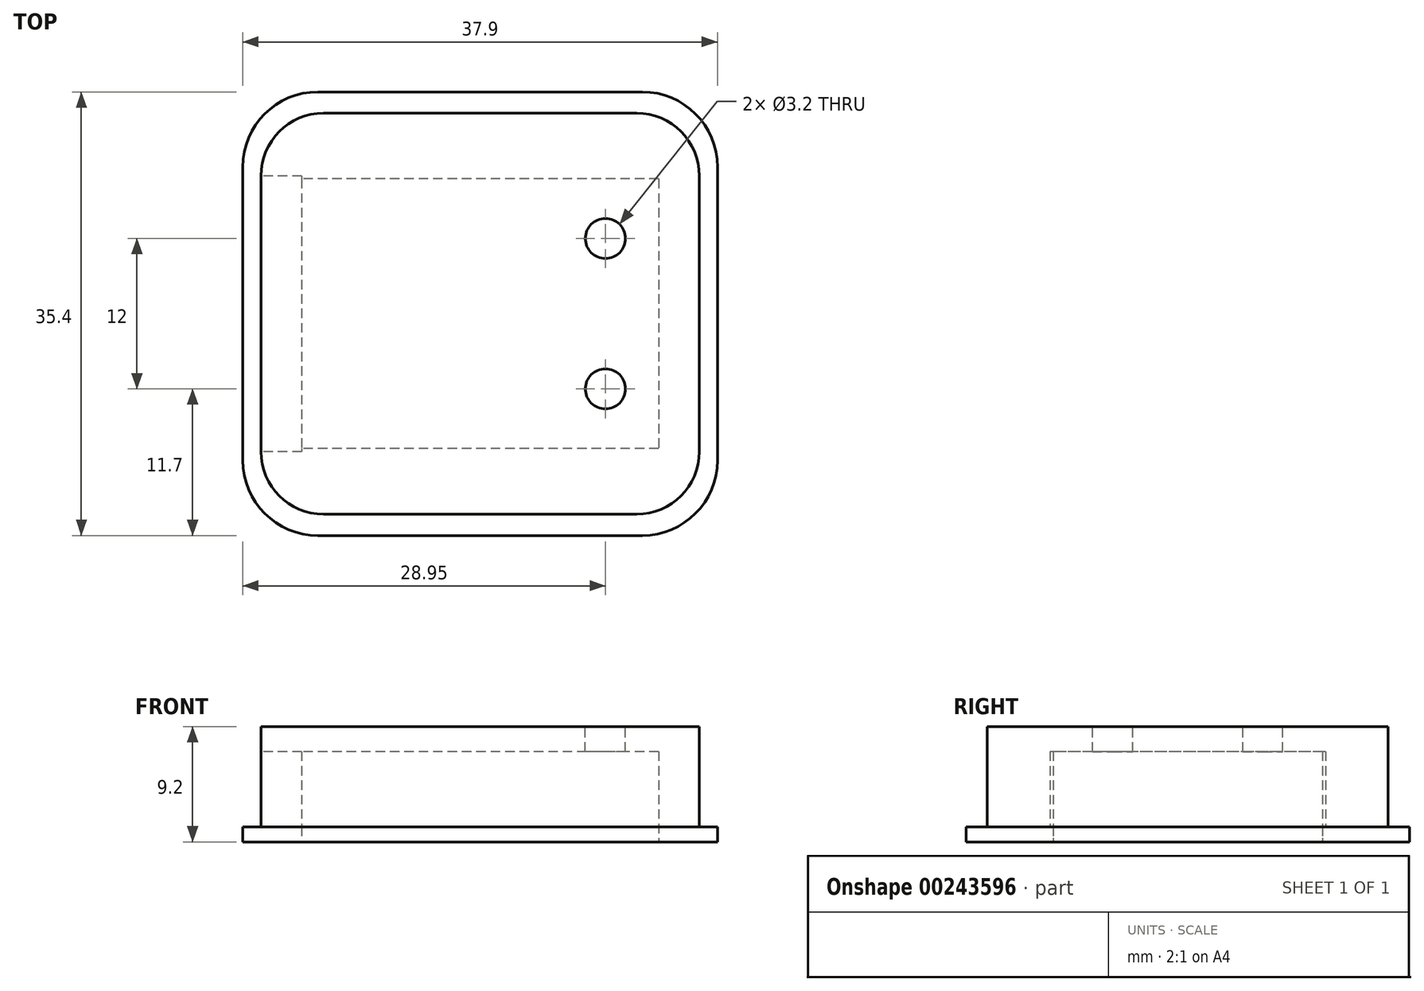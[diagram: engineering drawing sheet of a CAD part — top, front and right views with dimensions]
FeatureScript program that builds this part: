
annotation { "Feature Type Name" : "Feature", "Feature Type Description" : "" }
export const myFeature = defineFeature(function(context is Context, id is Id, definition is map)
    precondition{}
    {
        {
            var Q0;
            Q0=qCreatedBy(makeId("Top.planeOp"),FACE);
            var sketch = newSketch(context, id + "F0", { "sketchPlane" : qUnion([Q0])});
            skLineSegment(sketch, "E0.bottom", {"start": v(21.25, 20) * mm, "end": v(-21.25, 20) * mm, "construction": true});
            skLineSegment(sketch, "E0.top", {"start": v(21.25, -20) * mm, "end": v(-21.25, -20) * mm, "construction": true});
            skLineSegment(sketch, "E0.left", {"start": v(21.25, 20) * mm, "end": v(21.25, -20) * mm, "construction": true});
            skLineSegment(sketch, "E0.right", {"start": v(-21.25, 20) * mm, "end": v(-21.25, -20) * mm, "construction": true});
            skPoint(sketch, "E0.middle", {"position": v(0, 0) * mm});
            skLineSegment(sketch, "E1.bottom", {"start": v(12.95, 17.7) * mm, "end": v(-12.95, 17.7) * mm});
            skLineSegment(sketch, "E1.top", {"start": v(12.95, -17.7) * mm, "end": v(-12.95, -17.7) * mm});
            skLineSegment(sketch, "E1.left", {"start": v(18.95, 11.7) * mm, "end": v(18.95, -11.7) * mm});
            skLineSegment(sketch, "E1.right", {"start": v(-18.95, 11.7) * mm, "end": v(-18.95, -11.7) * mm});
            skLineSegment(sketch, "E2.bottom", {"start": v(14.25, 10.75) * mm, "end": v(-14.25, 10.75) * mm});
            skLineSegment(sketch, "E2.top", {"start": v(14.25, -10.75) * mm, "end": v(-14.25, -10.75) * mm});
            skLineSegment(sketch, "E2.left", {"start": v(14.25, 10.75) * mm, "end": v(14.25, -10.75) * mm});
            skLineSegment(sketch, "E2.right", {"start": v(-14.25, 10.75) * mm, "end": v(-14.25, -10.75) * mm});
            skPoint(sketch, "E3.visualSharp", {"position": v(-18.95, 17.7) * mm});
            skArc(sketch, "E3.filletArc", {"start": v(-12.95, 17.7) * mm, "mid": v(-17.2, 15.94) * mm, "end": v(-18.95, 11.7) * mm});
            skPoint(sketch, "E4.visualSharp", {"position": v(18.95, 17.7) * mm});
            skArc(sketch, "E4.filletArc", {"start": v(18.95, 11.7) * mm, "mid": v(17.2, 15.94) * mm, "end": v(12.95, 17.7) * mm});
            skPoint(sketch, "E5.visualSharp", {"position": v(18.95, -17.7) * mm});
            skArc(sketch, "E5.filletArc", {"start": v(12.95, -17.7) * mm, "mid": v(17.2, -15.94) * mm, "end": v(18.95, -11.7) * mm});
            skPoint(sketch, "E6.visualSharp", {"position": v(-18.95, -17.7) * mm});
            skArc(sketch, "E6.filletArc", {"start": v(-18.95, -11.7) * mm, "mid": v(-17.2, -15.94) * mm, "end": v(-12.95, -17.7) * mm});
            skSolve(sketch);
        }
        {
            var Q0;
            Q0=qSketchRegion(id+"F0",true);
            extrude(context, id + "F1", {"entities" : qUnion([Q0]), "depth" : 1.2 * mm});
        }
        {
            var Q0;
            Q0=makeQuery(id+"F1.opExtrude","CAP_FACE",FACE,{"disambiguationData":[OSD([sQuery(id+"F0.wireOp",EDGE,"E1.bottom"),sQuery(id+"F0.wireOp",EDGE,"E1.top"),sQuery(id+"F0.wireOp",EDGE,"E1.left"),sQuery(id+"F0.wireOp",EDGE,"E1.right"),sQuery(id+"F0.wireOp",EDGE,"E2.bottom"),sQuery(id+"F0.wireOp",EDGE,"E2.top"),sQuery(id+"F0.wireOp",EDGE,"E2.left"),sQuery(id+"F0.wireOp",EDGE,"E2.right"),sQuery(id+"F0.wireOp",EDGE,"E3.filletArc"),sQuery(id+"F0.wireOp",EDGE,"E4.filletArc"),sQuery(id+"F0.wireOp",EDGE,"E5.filletArc"),sQuery(id+"F0.wireOp",EDGE,"E6.filletArc")])],"isStart":false});
            var sketch = newSketch(context, id + "F2", { "sketchPlane" : qUnion([Q0])});
            skLineSegment(sketch, "E7.bottom", {"start": v(14.25, 10.75) * mm, "end": v(-14.25, 10.75) * mm});
            skLineSegment(sketch, "E7.top", {"start": v(14.25, -10.75) * mm, "end": v(-14.25, -10.75) * mm});
            skLineSegment(sketch, "E7.left", {"start": v(14.25, 10.75) * mm, "end": v(14.25, -10.75) * mm});
            skLineSegment(sketch, "E7.right", {"start": v(-14.25, 10.75) * mm, "end": v(-14.25, -10.75) * mm});
            skPoint(sketch, "E7.middle", {"position": v(0, 0) * mm});
            skLineSegment(sketch, "E8.bottom", {"start": v(12.5, 16) * mm, "end": v(-12.5, 16) * mm});
            skLineSegment(sketch, "E8.top", {"start": v(12.5, -16) * mm, "end": v(-12.5, -16) * mm});
            skLineSegment(sketch, "E8.left", {"start": v(17.5, 11) * mm, "end": v(17.5, -11) * mm});
            skLineSegment(sketch, "E8.right", {"start": v(-17.5, 11) * mm, "end": v(-17.5, -11) * mm});
            skPoint(sketch, "E9.visualSharp", {"position": v(-17.5, 16) * mm});
            skArc(sketch, "E9.filletArc", {"start": v(-12.5, 16) * mm, "mid": v(-16.04, 14.54) * mm, "end": v(-17.5, 11) * mm});
            skPoint(sketch, "E10.visualSharp", {"position": v(-17.5, -16) * mm});
            skArc(sketch, "E10.filletArc", {"start": v(-17.5, -11) * mm, "mid": v(-16.04, -14.54) * mm, "end": v(-12.5, -16) * mm});
            skPoint(sketch, "E11.visualSharp", {"position": v(17.5, -16) * mm});
            skArc(sketch, "E11.filletArc", {"start": v(12.5, -16) * mm, "mid": v(16.04, -14.54) * mm, "end": v(17.5, -11) * mm});
            skPoint(sketch, "E12.visualSharp", {"position": v(17.5, 16) * mm});
            skArc(sketch, "E12.filletArc", {"start": v(17.5, 11) * mm, "mid": v(16.04, 14.54) * mm, "end": v(12.5, 16) * mm});
            skSolve(sketch);
        }
        {
            var Q0;
            Q0=qSketchRegion(id+"F2",true);
            extrude(context, id + "F3", {"entities" : qUnion([Q0]), "operationType" : NewBodyOperationType.ADD, "depth" : 6 * mm});
        }
        {
            var Q0;
            Q0=makeQuery(id+"F3.opExtrude","CAP_FACE",FACE,{"disambiguationData":[OSD([sQuery(id+"F2.wireOp",EDGE,"E7.bottom"),sQuery(id+"F2.wireOp",EDGE,"E7.top"),sQuery(id+"F2.wireOp",EDGE,"E7.left"),sQuery(id+"F2.wireOp",EDGE,"E7.right"),sQuery(id+"F2.wireOp",EDGE,"E8.bottom"),sQuery(id+"F2.wireOp",EDGE,"E8.top"),sQuery(id+"F2.wireOp",EDGE,"E8.left"),sQuery(id+"F2.wireOp",EDGE,"E8.right"),sQuery(id+"F2.wireOp",EDGE,"E9.filletArc"),sQuery(id+"F2.wireOp",EDGE,"E10.filletArc"),sQuery(id+"F2.wireOp",EDGE,"E11.filletArc"),sQuery(id+"F2.wireOp",EDGE,"E12.filletArc")])],"isStart":false});
            var sketch = newSketch(context, id + "F4", { "sketchPlane" : qUnion([Q0])});
            skLineSegment(sketch, "E13.bottom", {"start": v(12.5, 16) * mm, "end": v(-12.5, 16) * mm});
            skLineSegment(sketch, "E13.top", {"start": v(12.5, -16) * mm, "end": v(-12.5, -16) * mm});
            skLineSegment(sketch, "E13.left", {"start": v(17.5, 11) * mm, "end": v(17.5, -11) * mm});
            skLineSegment(sketch, "E13.right", {"start": v(-17.5, 11) * mm, "end": v(-17.5, -11) * mm});
            skPoint(sketch, "E13.middle", {"position": v(0, 0) * mm});
            skPoint(sketch, "E14.visualSharp", {"position": v(-17.5, 16) * mm});
            skArc(sketch, "E14.filletArc", {"start": v(-12.5, 16) * mm, "mid": v(-16.04, 14.54) * mm, "end": v(-17.5, 11) * mm});
            skPoint(sketch, "E15.visualSharp", {"position": v(17.5, 16) * mm});
            skArc(sketch, "E15.filletArc", {"start": v(17.5, 11) * mm, "mid": v(16.04, 14.54) * mm, "end": v(12.5, 16) * mm});
            skPoint(sketch, "E16.visualSharp", {"position": v(17.5, -16) * mm});
            skArc(sketch, "E16.filletArc", {"start": v(12.5, -16) * mm, "mid": v(16.04, -14.54) * mm, "end": v(17.5, -11) * mm});
            skPoint(sketch, "E17.visualSharp", {"position": v(-17.5, -16) * mm});
            skArc(sketch, "E17.filletArc", {"start": v(-17.5, -11) * mm, "mid": v(-16.04, -14.54) * mm, "end": v(-12.5, -16) * mm});
            skSolve(sketch);
        }
        {
            var Q0;
            Q0 = qSketchRegion(id + "F4", true);
            extrude(context, id + "F5", {"entities" : qUnion([Q0]), "operationType" : NewBodyOperationType.ADD, "depth" : 2 * mm});
        }
        {
            var Q0;
            Q0=makeQuery(id+"F5.boolean.opBoolean","MERGE",FACE,{"derivedFrom":[makeQuery(id+"F3.opExtrude","SWEPT_FACE",FACE,{"disambiguationData":[OSD([sQuery(id+"F2.wireOp",EDGE,"E8.right")])]}),makeQuery(id+"F5.opExtrude","SWEPT_FACE",FACE,{"disambiguationData":[OSD([sQuery(id+"F4.wireOp",EDGE,"E13.right")])]})]});
            var sketch = newSketch(context, id + "F6", { "sketchPlane" : qUnion([Q0])});
            skLineSegment(sketch, "E18.bottom", {"start": v(-11, 7.2) * mm, "end": v(11, 7.2) * mm});
            skLineSegment(sketch, "E18.top", {"start": v(-11, 1.2) * mm, "end": v(11, 1.2) * mm});
            skLineSegment(sketch, "E18.left", {"start": v(-11, 7.2) * mm, "end": v(-11, 1.2) * mm});
            skLineSegment(sketch, "E18.right", {"start": v(11, 7.2) * mm, "end": v(11, 1.2) * mm});
            skSolve(sketch);
        }
        {
            var Q0;
            Q0 = qSketchRegion(id + "F6", true);
            var Q1;
            Q1=makeQuery(id+"F3.boolean.opBoolean","MERGE",FACE,{"derivedFrom":[makeQuery(id+"F1.opExtrude","SWEPT_FACE",FACE,{"disambiguationData":[OSD([sQuery(id+"F0.wireOp",EDGE,"E2.right")])]}),makeQuery(id+"F3.opExtrude","SWEPT_FACE",FACE,{"disambiguationData":[OSD([sQuery(id+"F2.wireOp",EDGE,"E7.right")])]})]});
            extrude(context, id + "F7", {"entities" : qUnion([Q0]), "operationType" : NewBodyOperationType.REMOVE, "endBound" : BoundingType.UP_TO_SURFACE, "oppositeDirection" : true, "endBoundEntityFace" : qUnion([Q1]), "depth" : 25 * mm});
        }
        {
            var Q0;
            Q0=makeQuery(id+"F5.opExtrude","CAP_FACE",FACE,{"disambiguationData":[OSD([sQuery(id+"F4.wireOp",EDGE,"E13.bottom"),sQuery(id+"F4.wireOp",EDGE,"E13.top"),sQuery(id+"F4.wireOp",EDGE,"E13.left"),sQuery(id+"F4.wireOp",EDGE,"E13.right"),sQuery(id+"F4.wireOp",EDGE,"E14.filletArc"),sQuery(id+"F4.wireOp",EDGE,"E15.filletArc"),sQuery(id+"F4.wireOp",EDGE,"E16.filletArc"),sQuery(id+"F4.wireOp",EDGE,"E17.filletArc")])],"isStart":false});
            var sketch = newSketch(context, id + "F8", { "sketchPlane" : qUnion([Q0])});
            skLineSegment(sketch, "E19", {"start": v(0, 0) * mm, "end": v(26.53, 0) * mm, "construction": true});
            skLineSegment(sketch, "E20", {"start": v(26.53, 0) * mm, "end": v(26.53, -0.33) * mm, "construction": true});
            skCircle(sketch, "E21", {"center": v(10, 6) * mm, "radius": 1.6 * mm});
            skCircle(sketch, "E22.MirrorC", {"center": v(10, -6) * mm, "radius": 1.6 * mm});
            skSolve(sketch);
        }
        {
            var Q0;
            Q0 = qSketchRegion(id + "F8", true);
            var Q1;
            Q1=makeQuery(id+"F7.boolean.opBoolean","MERGE",FACE,{"derivedFrom":[makeQuery(id+"F5.opExtrude","CAP_FACE",FACE,{"disambiguationData":[OSD([sQuery(id+"F4.wireOp",EDGE,"E13.bottom"),sQuery(id+"F4.wireOp",EDGE,"E13.top"),sQuery(id+"F4.wireOp",EDGE,"E13.left"),sQuery(id+"F4.wireOp",EDGE,"E13.right"),sQuery(id+"F4.wireOp",EDGE,"E14.filletArc"),sQuery(id+"F4.wireOp",EDGE,"E15.filletArc"),sQuery(id+"F4.wireOp",EDGE,"E16.filletArc"),sQuery(id+"F4.wireOp",EDGE,"E17.filletArc")])],"isStart":true}),makeQuery(id+"F7.opExtrude","SWEPT_FACE",FACE,{"disambiguationData":[OSD([sQuery(id+"F6.wireOp",EDGE,"E18.bottom")])]})]});
            extrude(context, id + "F9", {"entities" : qUnion([Q0]), "operationType" : NewBodyOperationType.REMOVE, "endBound" : BoundingType.UP_TO_SURFACE, "oppositeDirection" : true, "endBoundEntityFace" : qUnion([Q1]), "depth" : 25 * mm});
        }
    });
